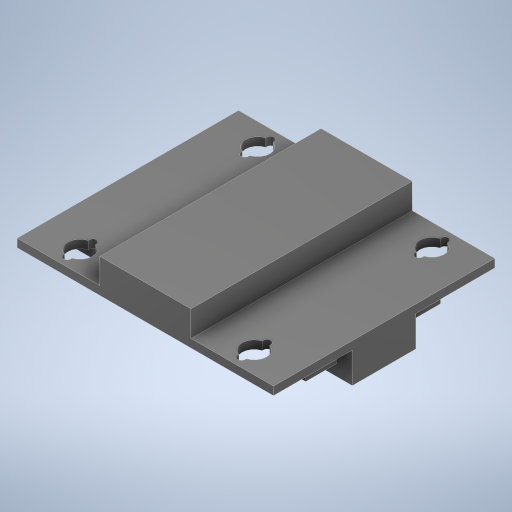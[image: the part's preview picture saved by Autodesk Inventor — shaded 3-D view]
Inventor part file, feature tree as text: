
AUTODESK INVENTOR PART (.ipt)
format: ipt  version: 2024.2 (Build 282272000, 272)  size: 323,072 bytes
history: native  units: mm
features: extrude x4, other x1, sketch x1
ambient origin geometry x8: Origin, YZ Plane, XZ Plane, XY Plane, X Axis, Y Axis, Z Axis, Center Point
bodies: Body1 (feature_tree)
feature tree (6):
  other  "ソリッド1"
  sketch  "スケッチ1"
  extrude  "押し出し1"  Depth=50.0mm
  extrude  "押し出し2"  Depth=43.18mm
  extrude  "押し出し3"  Depth=34.0mm
  extrude  "Extrusion4"  Depth=34.68mm
